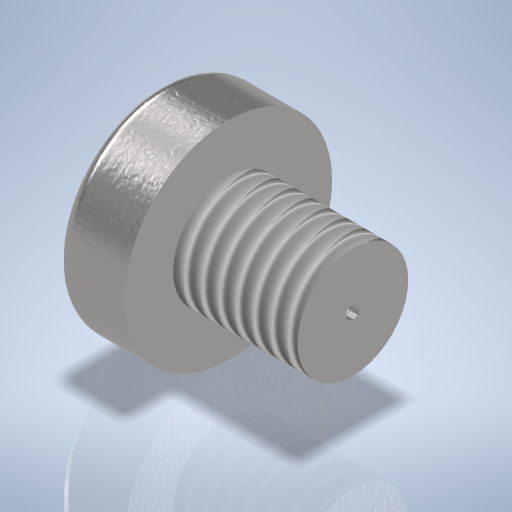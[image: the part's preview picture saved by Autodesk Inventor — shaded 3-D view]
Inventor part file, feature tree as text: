
AUTODESK INVENTOR PART (.ipt)
format: ipt  version: 2024 (Build 280153000, 153)  size: 331,776 bytes
history: native  units: mm
features: sketch x2, revolve x1, thread x1, hole x1, fillet x1
ambient origin geometry x8: Origin, YZ Plane, XZ Plane, XY Plane, X Axis, Y Axis, Z Axis, Center Point
bodies: Volumenkörper1 (feature_tree)
feature tree (6):
  revolve  "Umdrehung1"
  thread  "Gewinde1"  [1 undecoded]
  hole  "Bohrung1"  [1 undecoded]
  fillet  "Rundung1"  Radius=8.0mm
  sketch  "Skizze1"  dims[d1=9.0mm d2=5.0mm d3=8.0mm]
  sketch  "Skizze2"  dims[d4=90.0deg d5=11.0mm d6=0.0mm d7=1.0mm d8=10.0mm d9=4.0mm d10=2.0mm d11=90.0deg d12=8.0mm d13=0.0mm d14=1.0mm]
note: 2 required parameter values undecoded (feature->parameter linkage not recoverable at this tier; creation-order binding heuristic only, values carry confidence <= 0.55)
